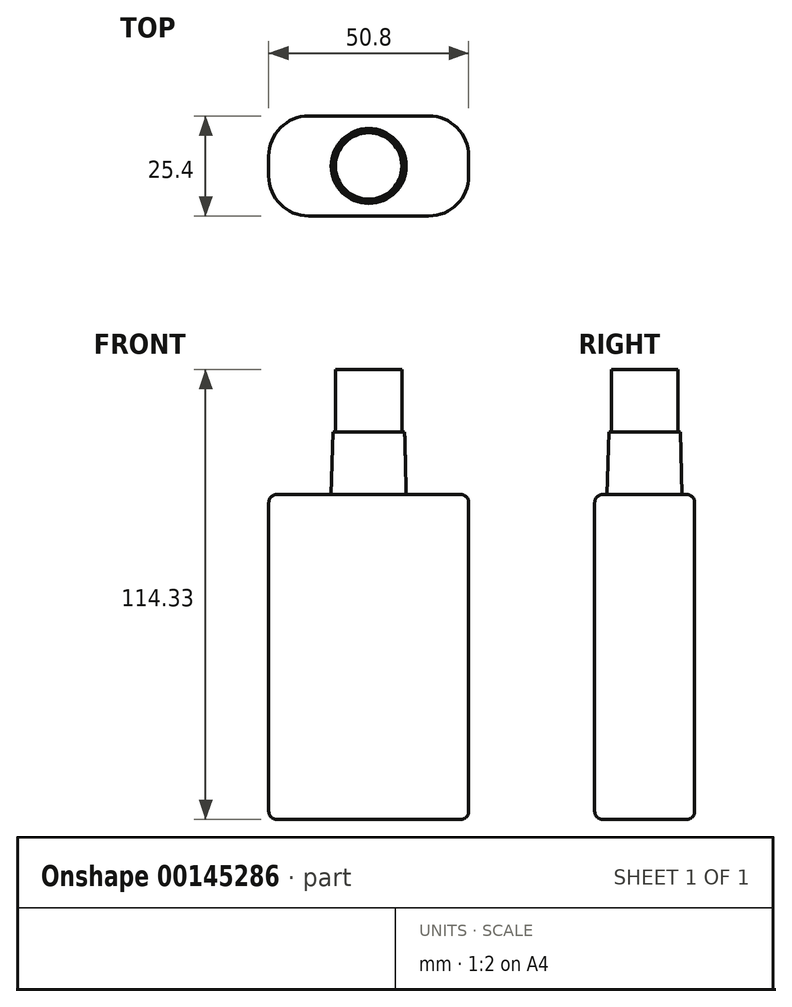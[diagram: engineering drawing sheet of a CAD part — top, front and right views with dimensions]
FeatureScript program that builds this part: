
annotation { "Feature Type Name" : "Feature", "Feature Type Description" : "" }
export const myFeature = defineFeature(function(context is Context, id is Id, definition is map)
    precondition{}
    {
        {
            var Q0;
            Q0=qCreatedBy(makeId("Top.planeOp"),FACE);
            var sketch = newSketch(context, id + "F0", { "sketchPlane" : qUnion([Q0])});
            skLineSegment(sketch, "E0.bottom", {"start": v(15.24, 12.7) * mm, "end": v(-15.24, 12.7) * mm});
            skLineSegment(sketch, "E0.top", {"start": v(15.24, -12.7) * mm, "end": v(-15.24, -12.7) * mm});
            skLineSegment(sketch, "E0.left", {"start": v(25.4, 2.54) * mm, "end": v(25.4, -2.54) * mm});
            skLineSegment(sketch, "E0.right", {"start": v(-25.4, 2.54) * mm, "end": v(-25.4, -2.54) * mm});
            skPoint(sketch, "E0.middle", {"position": v(0, 0) * mm});
            skPoint(sketch, "E1.visualSharp", {"position": v(-25.4, -12.7) * mm});
            skArc(sketch, "E1.filletArc", {"start": v(-25.4, -2.54) * mm, "mid": v(-22.42, -9.72) * mm, "end": v(-15.24, -12.7) * mm});
            skPoint(sketch, "E2.visualSharp", {"position": v(-25.4, 12.7) * mm});
            skArc(sketch, "E2.filletArc", {"start": v(-15.24, 12.7) * mm, "mid": v(-22.42, 9.72) * mm, "end": v(-25.4, 2.54) * mm});
            skPoint(sketch, "E3.visualSharp", {"position": v(25.4, 12.7) * mm});
            skArc(sketch, "E3.filletArc", {"start": v(25.4, 2.54) * mm, "mid": v(22.42, 9.72) * mm, "end": v(15.24, 12.7) * mm});
            skPoint(sketch, "E4.visualSharp", {"position": v(25.4, -12.7) * mm});
            skArc(sketch, "E4.filletArc", {"start": v(15.24, -12.7) * mm, "mid": v(22.42, -9.72) * mm, "end": v(25.4, -2.54) * mm});
            skSolve(sketch);
        }
        {
            var Q0;
            Q0=makeQuery(id+"F0.imprint","IMPRINT",FACE,{"disambiguationData":[TD([[makeQuery(id+"F0.imprint","IMPRINT",EDGE,{"derivedFrom":sQuery(id+"F0.wireOp",EDGE,"E0.bottom")}),1.0]])]});
            extrude(context, id + "F1", {"entities" : qUnion([Q0]), "depth" : 82.55 * mm});
        }
        {
            var Q0;
            Q0=makeQuery(id+"F1.opExtrude","CAP_FACE",FACE,{"disambiguationData":[OSD([sQuery(id+"F0.wireOp",EDGE,"E0.bottom"),sQuery(id+"F0.wireOp",EDGE,"E0.top"),sQuery(id+"F0.wireOp",EDGE,"E0.left"),sQuery(id+"F0.wireOp",EDGE,"E0.right"),sQuery(id+"F0.wireOp",EDGE,"E1.filletArc"),sQuery(id+"F0.wireOp",EDGE,"E2.filletArc"),sQuery(id+"F0.wireOp",EDGE,"E3.filletArc"),sQuery(id+"F0.wireOp",EDGE,"E4.filletArc")])],"isStart":false});
            var sketch = newSketch(context, id + "F2", { "sketchPlane" : qUnion([Q0])});
            skCircle(sketch, "E5", {"center": v(0, 0) * mm, "radius": 9.53 * mm});
            skSolve(sketch);
        }
        {
            var Q0;
            Q0=makeQuery(id+"F2.imprint","IMPRINT",FACE,{"disambiguationData":[TD([[makeQuery(id+"F2.imprint","IMPRINT",EDGE,{"derivedFrom":sQuery(id+"F2.wireOp",EDGE,"E5")}),1.0]])]});
            extrude(context, id + "F3", {"entities" : qUnion([Q0]), "depth" : 15.88 * mm, "hasDraft" : true, "draftAngle" : 1.5 * degree, "draftPullDirection" : true});
        }
        {
            var Q0;
            Q0=qCreatedBy(makeId("Front.planeOp"),FACE);
            var sketch = newSketch(context, id + "F4", { "sketchPlane" : qUnion([Q0])});
            skLineSegment(sketch, "E6", {"start": v(0, 114.33) * mm, "end": v(8.43, 114.33) * mm});
            skLineSegment(sketch, "E7", {"start": v(8.43, 114.33) * mm, "end": v(8.43, 98.43) * mm});
            skLineSegment(sketch, "E8", {"start": v(0, 114.33) * mm, "end": v(0, 98.43) * mm});
            skLineSegment(sketch, "E9", {"start": v(0, 98.43) * mm, "end": v(8.43, 98.43) * mm});
            skSolve(sketch);
        }
        {
            var Q0;
            Q0=makeQuery(id+"F4.imprint","IMPRINT",FACE,{"disambiguationData":[TD([[makeQuery(id+"F4.imprint","IMPRINT",EDGE,{"derivedFrom":sQuery(id+"F4.wireOp",EDGE,"E6")}),-1.0]])]});
            var Q1;
            Q1=sQuery(id+"F4.wireOp",EDGE,"E8");
            revolve(context, id + "F5", {"operationType" : NewBodyOperationType.ADD, "entities" : qUnion([Q0]), "axis" : qUnion([Q1]), "revolveType" : RevolveType.FULL});
        }
        {
            var Q0;
            Q0=makeQuery(id+"F1.opExtrude","CAP_FACE",FACE,{"disambiguationData":[OSD([sQuery(id+"F0.wireOp",EDGE,"E0.bottom"),sQuery(id+"F0.wireOp",EDGE,"E0.top"),sQuery(id+"F0.wireOp",EDGE,"E0.left"),sQuery(id+"F0.wireOp",EDGE,"E0.right"),sQuery(id+"F0.wireOp",EDGE,"E1.filletArc"),sQuery(id+"F0.wireOp",EDGE,"E2.filletArc"),sQuery(id+"F0.wireOp",EDGE,"E3.filletArc"),sQuery(id+"F0.wireOp",EDGE,"E4.filletArc")])],"isStart":false});
            var Q1;
            Q1=makeQuery(id+"F1.opExtrude","CAP_EDGE",EDGE,{"disambiguationData":[OSD([sQuery(id+"F0.wireOp",EDGE,"E0.bottom")])],"isStart":true});
            fillet(context, id + "F6", {"entities" : qUnion([Q0, Q1]), "radius" : 2.03 * mm, "tangentPropagation" : true, "allowEdgeOverflow" : false});
        }
    });
